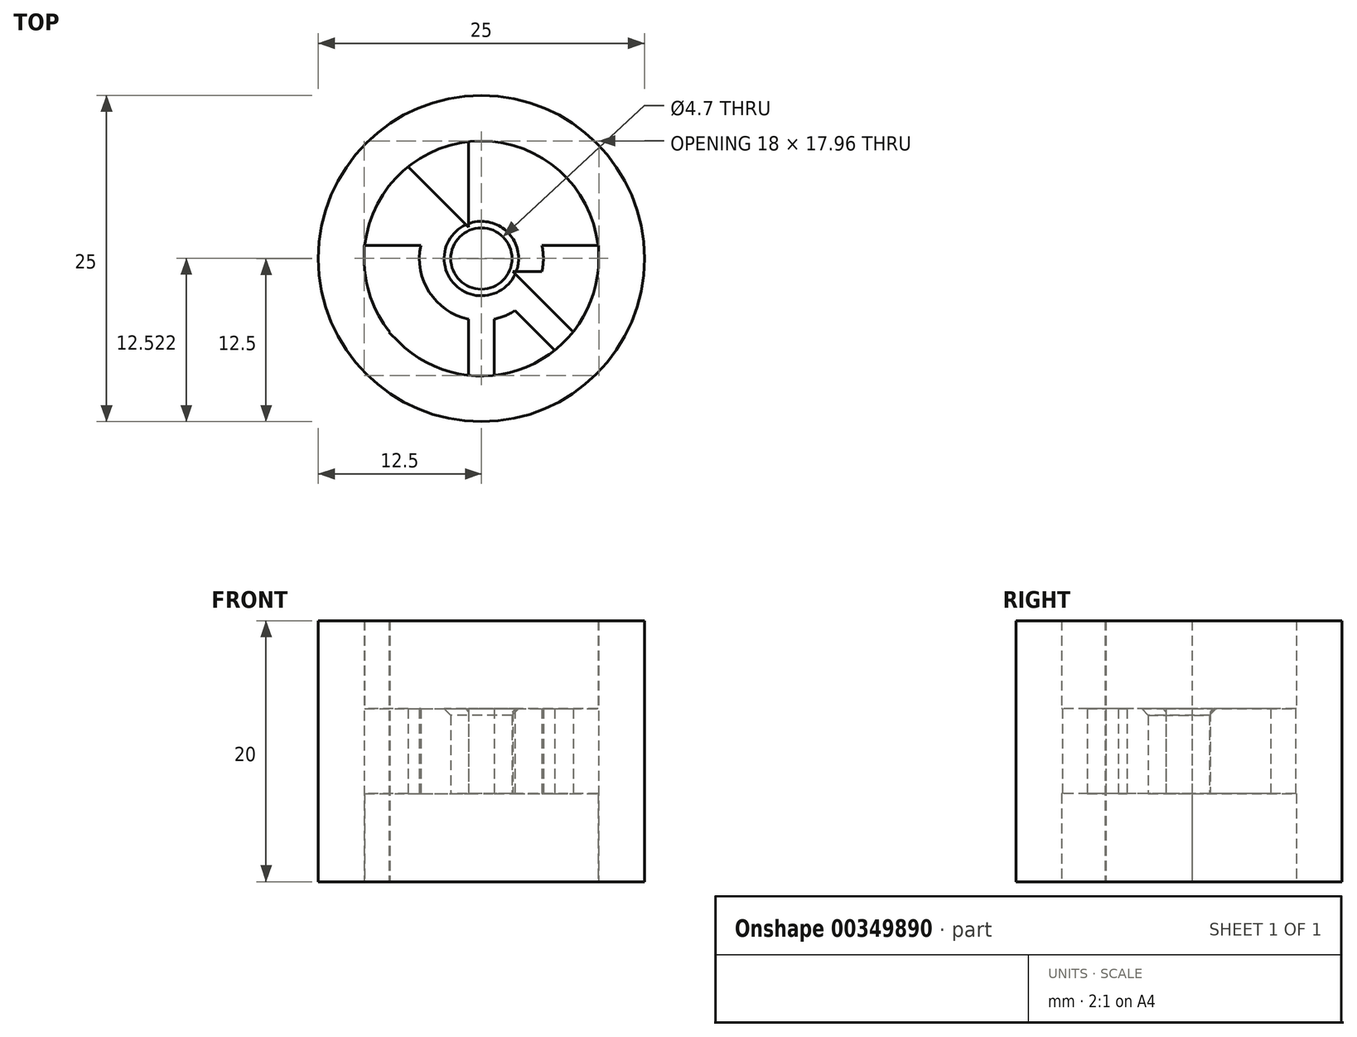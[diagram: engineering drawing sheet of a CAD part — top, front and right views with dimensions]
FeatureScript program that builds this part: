
annotation { "Feature Type Name" : "Feature", "Feature Type Description" : "" }
export const myFeature = defineFeature(function(context is Context, id is Id, definition is map)
    precondition{}
    {
        {
            var Q0;
            Q0=qCreatedBy(makeId("Top.planeOp"),FACE);
            var sketch = newSketch(context, id + "F0", { "sketchPlane" : qUnion([Q0])});
            skCircle(sketch, "E0", {"center": v(0, 0) * mm, "radius": 2.35 * mm});
            skCircle(sketch, "E1", {"center": v(0, 0) * mm, "radius": 12.5 * mm});
            skCircle(sketch, "E2", {"center": v(0, 0) * mm, "radius": 9 * mm});
            skCircle(sketch, "E3", {"center": v(0, 0) * mm, "radius": 4.75 * mm});
            skPoint(sketch, "E4", {"position": v(0, 9) * mm});
            skPoint(sketch, "E5", {"position": v(0, -9) * mm});
            skPoint(sketch, "E6", {"position": v(9, 0) * mm});
            skPoint(sketch, "E7", {"position": v(-9, 0) * mm});
            skLineSegment(sketch, "E8.bottom", {"start": v(-1, 9) * mm, "end": v(1, 9) * mm});
            skLineSegment(sketch, "E8.top", {"start": v(-1, -9) * mm, "end": v(1, -9) * mm});
            skLineSegment(sketch, "E8.left", {"start": v(-1, 9) * mm, "end": v(-1, -9) * mm});
            skLineSegment(sketch, "E8.right", {"start": v(1, 9) * mm, "end": v(1, -9) * mm});
            skLineSegment(sketch, "E9.bottom", {"start": v(-9, 1) * mm, "end": v(9, 1) * mm});
            skLineSegment(sketch, "E9.top", {"start": v(-9, -1) * mm, "end": v(9, -1) * mm});
            skLineSegment(sketch, "E9.left", {"start": v(-9, 1) * mm, "end": v(-9, -1) * mm});
            skLineSegment(sketch, "E9.right", {"start": v(9, 1) * mm, "end": v(9, -1) * mm});
            skLineSegment(sketch, "E10", {"start": v(0, 0) * mm, "end": v(-6.36, -6.36) * mm, "construction": true});
            skLineSegment(sketch, "E11", {"start": v(0, 0) * mm, "end": v(-6.36, 6.36) * mm, "construction": true});
            skLineSegment(sketch, "E12", {"start": v(0, 0) * mm, "end": v(6.36, 6.36) * mm, "construction": true});
            skLineSegment(sketch, "E13", {"start": v(0, 0) * mm, "end": v(6.36, -6.36) * mm, "construction": true});
            skPoint(sketch, "E14", {"position": v(-1, -1) * mm});
            skPoint(sketch, "E15", {"position": v(-1, 1) * mm});
            skLineSegment(sketch, "E16", {"start": v(-7.07, -5.66) * mm, "end": v(-5.66, -7.07) * mm});
            skPoint(sketch, "E17", {"position": v(-6.36, -6.36) * mm});
            skLineSegment(sketch, "E18", {"start": v(5.66, -7.07) * mm, "end": v(7.07, -5.66) * mm});
            skPoint(sketch, "E19", {"position": v(6.36, -6.36) * mm});
            skPoint(sketch, "E20", {"position": v(6.36, 6.36) * mm});
            skLineSegment(sketch, "E21", {"start": v(5.66, 7.07) * mm, "end": v(7.07, 5.66) * mm});
            skLineSegment(sketch, "E22", {"start": v(-7.07, -5.66) * mm, "end": v(5.66, 7.07) * mm});
            skLineSegment(sketch, "E23", {"start": v(7.07, 5.66) * mm, "end": v(-5.66, -7.07) * mm});
            skLineSegment(sketch, "E24", {"start": v(-7.07, 5.66) * mm, "end": v(-5.66, 7.07) * mm});
            skPoint(sketch, "E25", {"position": v(-6.36, 6.36) * mm});
            skLineSegment(sketch, "E26", {"start": v(-7.07, 5.66) * mm, "end": v(5.66, -7.07) * mm});
            skLineSegment(sketch, "E27", {"start": v(-5.66, 7.07) * mm, "end": v(7.07, -5.66) * mm});
            skSolve(sketch);
        }
        {
            var Q0;
            {var subQ0=sQuery(id+"F0.wireOp",EDGE,"E8.right");var subQ5=sQuery(id+"F0.wireOp",EDGE,"E2");var subQ6=makeQuery(id+"F0.imprint","INTERSECT",VERTEX,{"disambiguationData":[OD(0.0)],"derivedFrom":[subQ5,subQ0]});Q0=makeQuery(id+"F0.imprint","IMPRINT",FACE,{"disambiguationData":[TD([[makeQuery(id+"F0.imprint","IMPRINT",EDGE,{"disambiguationData":[TD([[subQ6,-1.0]])],"derivedFrom":subQ5}),1.0]])]});}
            var Q1;
            {var subQ3=sQuery(id+"F0.wireOp",EDGE,"E22");var subQ7=sQuery(id+"F0.wireOp",EDGE,"E0");var subQ8=makeQuery(id+"F0.imprint","INTERSECT",VERTEX,{"disambiguationData":[OD(0.0)],"derivedFrom":[subQ7,subQ3]});Q1=makeQuery(id+"F0.imprint","IMPRINT",FACE,{"disambiguationData":[TD([[makeQuery(id+"F0.imprint","IMPRINT",EDGE,{"disambiguationData":[TD([[subQ8,-1.0]])],"derivedFrom":subQ7}),-1.0]])]});}
            var Q2;
            {var subQ0=sQuery(id+"F0.wireOp",EDGE,"E27");var subQ1=sQuery(id+"F0.wireOp",EDGE,"E0");var subQ2=makeQuery(id+"F0.imprint","INTERSECT",VERTEX,{"disambiguationData":[OD(0.0)],"derivedFrom":[subQ1,subQ0]});Q2=makeQuery(id+"F0.imprint","IMPRINT",FACE,{"disambiguationData":[TD([[makeQuery(id+"F0.imprint","IMPRINT",EDGE,{"disambiguationData":[TD([[subQ2,-1.0]])],"derivedFrom":subQ1}),-1.0]])]});}
            var Q3;
            {var subQ0=sQuery(id+"F0.wireOp",EDGE,"E8.right");var subQ1=sQuery(id+"F0.wireOp",EDGE,"E0");var subQ2=makeQuery(id+"F0.imprint","INTERSECT",VERTEX,{"disambiguationData":[OD(0.0)],"derivedFrom":[subQ1,subQ0]});Q3=makeQuery(id+"F0.imprint","IMPRINT",FACE,{"disambiguationData":[TD([[makeQuery(id+"F0.imprint","IMPRINT",EDGE,{"disambiguationData":[TD([[subQ2,-1.0]])],"derivedFrom":subQ1}),-1.0]])]});}
            var Q4;
            {var subQ1=sQuery(id+"F0.wireOp",EDGE,"E0");var subQ9=sQuery(id+"F0.wireOp",EDGE,"E9.bottom");var subQ10=makeQuery(id+"F0.imprint","INTERSECT",VERTEX,{"disambiguationData":[OD(0.0)],"derivedFrom":[subQ1,subQ9]});Q4=makeQuery(id+"F0.imprint","IMPRINT",FACE,{"disambiguationData":[TD([[makeQuery(id+"F0.imprint","IMPRINT",EDGE,{"disambiguationData":[TD([[subQ10,-1.0]])],"derivedFrom":subQ1}),-1.0]])]});}
            var Q5;
            {var subQ3=sQuery(id+"F0.wireOp",EDGE,"E23");var subQ9=sQuery(id+"F0.wireOp",EDGE,"E0");var subQ10=makeQuery(id+"F0.imprint","INTERSECT",VERTEX,{"disambiguationData":[OD(0.0)],"derivedFrom":[subQ9,subQ3]});Q5=makeQuery(id+"F0.imprint","IMPRINT",FACE,{"disambiguationData":[TD([[makeQuery(id+"F0.imprint","IMPRINT",EDGE,{"disambiguationData":[TD([[subQ10,1.0]])],"derivedFrom":subQ9}),-1.0]])]});}
            var Q6;
            {var subQ0=sQuery(id+"F0.wireOp",EDGE,"E9.bottom");var subQ1=sQuery(id+"F0.wireOp",EDGE,"E0");var subQ2=makeQuery(id+"F0.imprint","INTERSECT",VERTEX,{"disambiguationData":[OD(0.0)],"derivedFrom":[subQ1,subQ0]});Q6=makeQuery(id+"F0.imprint","IMPRINT",FACE,{"disambiguationData":[TD([[makeQuery(id+"F0.imprint","IMPRINT",EDGE,{"disambiguationData":[TD([[subQ2,1.0]])],"derivedFrom":subQ1}),-1.0]])]});}
            var Q7;
            {var subQ1=sQuery(id+"F0.wireOp",EDGE,"E0");var subQ9=sQuery(id+"F0.wireOp",EDGE,"E8.right");var subQ10=makeQuery(id+"F0.imprint","INTERSECT",VERTEX,{"disambiguationData":[OD(1.0)],"derivedFrom":[subQ1,subQ9]});Q7=makeQuery(id+"F0.imprint","IMPRINT",FACE,{"disambiguationData":[TD([[makeQuery(id+"F0.imprint","IMPRINT",EDGE,{"disambiguationData":[TD([[subQ10,-1.0]])],"derivedFrom":subQ1}),-1.0]])]});}
            var Q8;
            {var subQ0=sQuery(id+"F0.wireOp",EDGE,"E9.top");var subQ1=sQuery(id+"F0.wireOp",EDGE,"E0");var subQ2=makeQuery(id+"F0.imprint","INTERSECT",VERTEX,{"disambiguationData":[OD(1.0)],"derivedFrom":[subQ1,subQ0]});Q8=makeQuery(id+"F0.imprint","IMPRINT",FACE,{"disambiguationData":[TD([[makeQuery(id+"F0.imprint","IMPRINT",EDGE,{"disambiguationData":[TD([[subQ2,-1.0]])],"derivedFrom":subQ1}),-1.0]])]});}
            var Q9;
            {var subQ0=sQuery(id+"F0.wireOp",EDGE,"E26");var subQ1=sQuery(id+"F0.wireOp",EDGE,"E0");var subQ2=makeQuery(id+"F0.imprint","INTERSECT",VERTEX,{"disambiguationData":[OD(1.0)],"derivedFrom":[subQ1,subQ0]});Q9=makeQuery(id+"F0.imprint","IMPRINT",FACE,{"disambiguationData":[TD([[makeQuery(id+"F0.imprint","IMPRINT",EDGE,{"disambiguationData":[TD([[subQ2,-1.0]])],"derivedFrom":subQ1}),-1.0]])]});}
            var Q10;
            {var subQ0=sQuery(id+"F0.wireOp",EDGE,"E8.left");var subQ1=sQuery(id+"F0.wireOp",EDGE,"E0");var subQ2=makeQuery(id+"F0.imprint","INTERSECT",VERTEX,{"disambiguationData":[OD(0.0)],"derivedFrom":[subQ1,subQ0]});Q10=makeQuery(id+"F0.imprint","IMPRINT",FACE,{"disambiguationData":[TD([[makeQuery(id+"F0.imprint","IMPRINT",EDGE,{"disambiguationData":[TD([[subQ2,-1.0]])],"derivedFrom":subQ1}),-1.0]])]});}
            var Q11;
            {var subQ3=sQuery(id+"F0.wireOp",EDGE,"E26");var subQ9=sQuery(id+"F0.wireOp",EDGE,"E0");var subQ10=makeQuery(id+"F0.imprint","INTERSECT",VERTEX,{"disambiguationData":[OD(0.0)],"derivedFrom":[subQ9,subQ3]});Q11=makeQuery(id+"F0.imprint","IMPRINT",FACE,{"disambiguationData":[TD([[makeQuery(id+"F0.imprint","IMPRINT",EDGE,{"disambiguationData":[TD([[subQ10,-1.0]])],"derivedFrom":subQ9}),-1.0]])]});}
            var Q12;
            {var subQ0=sQuery(id+"F0.wireOp",EDGE,"E9.top");var subQ1=sQuery(id+"F0.wireOp",EDGE,"E0");var subQ2=makeQuery(id+"F0.imprint","INTERSECT",VERTEX,{"disambiguationData":[OD(0.0)],"derivedFrom":[subQ1,subQ0]});Q12=makeQuery(id+"F0.imprint","IMPRINT",FACE,{"disambiguationData":[TD([[makeQuery(id+"F0.imprint","IMPRINT",EDGE,{"disambiguationData":[TD([[subQ2,-1.0]])],"derivedFrom":subQ1}),-1.0]])]});}
            var Q13;
            {var subQ0=sQuery(id+"F0.wireOp",EDGE,"E9.bottom");var subQ1=sQuery(id+"F0.wireOp",EDGE,"E0");var subQ2=makeQuery(id+"F0.imprint","INTERSECT",VERTEX,{"disambiguationData":[OD(1.0)],"derivedFrom":[subQ1,subQ0]});Q13=makeQuery(id+"F0.imprint","IMPRINT",FACE,{"disambiguationData":[TD([[makeQuery(id+"F0.imprint","IMPRINT",EDGE,{"disambiguationData":[TD([[subQ2,-1.0]])],"derivedFrom":subQ1}),-1.0]])]});}
            var Q14;
            {var subQ0=sQuery(id+"F0.wireOp",EDGE,"E22");var subQ1=sQuery(id+"F0.wireOp",EDGE,"E0");var subQ2=makeQuery(id+"F0.imprint","INTERSECT",VERTEX,{"disambiguationData":[OD(1.0)],"derivedFrom":[subQ1,subQ0]});Q14=makeQuery(id+"F0.imprint","IMPRINT",FACE,{"disambiguationData":[TD([[makeQuery(id+"F0.imprint","IMPRINT",EDGE,{"disambiguationData":[TD([[subQ2,-1.0]])],"derivedFrom":subQ1}),-1.0]])]});}
            var Q15;
            {var subQ0=sQuery(id+"F0.wireOp",EDGE,"E8.left");var subQ1=sQuery(id+"F0.wireOp",EDGE,"E0");var subQ2=makeQuery(id+"F0.imprint","INTERSECT",VERTEX,{"disambiguationData":[OD(1.0)],"derivedFrom":[subQ1,subQ0]});Q15=makeQuery(id+"F0.imprint","IMPRINT",FACE,{"disambiguationData":[TD([[makeQuery(id+"F0.imprint","IMPRINT",EDGE,{"disambiguationData":[TD([[subQ2,-1.0]])],"derivedFrom":subQ1}),-1.0]])]});}
            var Q16;
            {var subQ7=sQuery(id+"F0.wireOp",EDGE,"E23");var subQ9=sQuery(id+"F0.wireOp",EDGE,"E0");var subQ10=makeQuery(id+"F0.imprint","INTERSECT",VERTEX,{"disambiguationData":[OD(1.0)],"derivedFrom":[subQ9,subQ7]});Q16=makeQuery(id+"F0.imprint","IMPRINT",FACE,{"disambiguationData":[TD([[makeQuery(id+"F0.imprint","IMPRINT",EDGE,{"disambiguationData":[TD([[subQ10,-1.0]])],"derivedFrom":subQ9}),-1.0]])]});}
            var Q17;
            {var subQ0=sQuery(id+"F0.wireOp",EDGE,"E23");var subQ5=sQuery(id+"F0.wireOp",EDGE,"E2");var subQ8=makeQuery(id+"F0.imprint","INTERSECT",VERTEX,{"disambiguationData":[OD(0.0)],"derivedFrom":[subQ5,subQ0]});Q17=makeQuery(id+"F0.imprint","IMPRINT",FACE,{"disambiguationData":[TD([[makeQuery(id+"F0.imprint","IMPRINT",EDGE,{"disambiguationData":[TD([[subQ8,-1.0]])],"derivedFrom":subQ5}),1.0]])]});}
            var Q18;
            {var subQ0=sQuery(id+"F0.wireOp",EDGE,"E9.bottom");var subQ1=sQuery(id+"F0.wireOp",EDGE,"E2");var subQ2=makeQuery(id+"F0.imprint","INTERSECT",VERTEX,{"disambiguationData":[OD(0.0)],"derivedFrom":[subQ1,subQ0]});Q18=makeQuery(id+"F0.imprint","IMPRINT",FACE,{"disambiguationData":[TD([[makeQuery(id+"F0.imprint","IMPRINT",EDGE,{"disambiguationData":[TD([[subQ2,1.0]])],"derivedFrom":subQ1}),1.0]])]});}
            var Q19;
            {var subQ0=sQuery(id+"F0.wireOp",EDGE,"E26");var subQ5=sQuery(id+"F0.wireOp",EDGE,"E2");var subQ8=makeQuery(id+"F0.imprint","INTERSECT",VERTEX,{"disambiguationData":[OD(1.0)],"derivedFrom":[subQ5,subQ0]});Q19=makeQuery(id+"F0.imprint","IMPRINT",FACE,{"disambiguationData":[TD([[makeQuery(id+"F0.imprint","IMPRINT",EDGE,{"disambiguationData":[TD([[subQ8,-1.0]])],"derivedFrom":subQ5}),1.0]])]});}
            var Q20;
            {var subQ0=sQuery(id+"F0.wireOp",EDGE,"E8.left");var subQ1=sQuery(id+"F0.wireOp",EDGE,"E2");var subQ2=makeQuery(id+"F0.imprint","INTERSECT",VERTEX,{"disambiguationData":[OD(1.0)],"derivedFrom":[subQ1,subQ0]});Q20=makeQuery(id+"F0.imprint","IMPRINT",FACE,{"disambiguationData":[TD([[makeQuery(id+"F0.imprint","IMPRINT",EDGE,{"disambiguationData":[TD([[subQ2,-1.0]])],"derivedFrom":subQ1}),1.0]])]});}
            var Q21;
            {var subQ0=sQuery(id+"F0.wireOp",EDGE,"E22");var subQ1=sQuery(id+"F0.wireOp",EDGE,"E2");var subQ2=makeQuery(id+"F0.imprint","INTERSECT",VERTEX,{"disambiguationData":[OD(1.0)],"derivedFrom":[subQ1,subQ0]});Q21=makeQuery(id+"F0.imprint","IMPRINT",FACE,{"disambiguationData":[TD([[makeQuery(id+"F0.imprint","IMPRINT",EDGE,{"disambiguationData":[TD([[subQ2,-1.0]])],"derivedFrom":subQ1}),1.0]])]});}
            var Q22;
            {var subQ0=sQuery(id+"F0.wireOp",EDGE,"E2");var subQ4=sQuery(id+"F0.wireOp",EDGE,"E9.bottom");var subQ5=makeQuery(id+"F0.imprint","INTERSECT",VERTEX,{"disambiguationData":[OD(1.0)],"derivedFrom":[subQ0,subQ4]});Q22=makeQuery(id+"F0.imprint","IMPRINT",FACE,{"disambiguationData":[TD([[makeQuery(id+"F0.imprint","IMPRINT",EDGE,{"disambiguationData":[TD([[subQ5,-1.0]])],"derivedFrom":subQ0}),1.0]])]});}
            var Q23;
            {var subQ1=sQuery(id+"F0.wireOp",EDGE,"E2");var subQ5=sQuery(id+"F0.wireOp",EDGE,"E27");var subQ8=makeQuery(id+"F0.imprint","INTERSECT",VERTEX,{"disambiguationData":[OD(0.0)],"derivedFrom":[subQ1,subQ5]});Q23=makeQuery(id+"F0.imprint","IMPRINT",FACE,{"disambiguationData":[TD([[makeQuery(id+"F0.imprint","IMPRINT",EDGE,{"disambiguationData":[TD([[subQ8,-1.0]])],"derivedFrom":subQ1}),1.0]])]});}
            var Q24;
            {var subQ0=sQuery(id+"F0.wireOp",EDGE,"E22");var subQ1=sQuery(id+"F0.wireOp",EDGE,"E3");var subQ2=makeQuery(id+"F0.imprint","INTERSECT",VERTEX,{"disambiguationData":[OD(0.0)],"derivedFrom":[subQ1,subQ0]});Q24=makeQuery(id+"F0.imprint","IMPRINT",FACE,{"disambiguationData":[TD([[makeQuery(id+"F0.imprint","IMPRINT",EDGE,{"disambiguationData":[TD([[subQ2,-1.0]])],"derivedFrom":subQ1}),1.0]])]});}
            var Q25;
            {var subQ0=sQuery(id+"F0.wireOp",EDGE,"E23");var subQ1=sQuery(id+"F0.wireOp",EDGE,"E3");var subQ2=makeQuery(id+"F0.imprint","INTERSECT",VERTEX,{"disambiguationData":[OD(0.0)],"derivedFrom":[subQ1,subQ0]});Q25=makeQuery(id+"F0.imprint","IMPRINT",FACE,{"disambiguationData":[TD([[makeQuery(id+"F0.imprint","IMPRINT",EDGE,{"disambiguationData":[TD([[subQ2,1.0]])],"derivedFrom":subQ1}),1.0]])]});}
            var Q26;
            {var subQ0=sQuery(id+"F0.wireOp",EDGE,"E27");var subQ1=sQuery(id+"F0.wireOp",EDGE,"E3");var subQ2=makeQuery(id+"F0.imprint","INTERSECT",VERTEX,{"disambiguationData":[OD(1.0)],"derivedFrom":[subQ1,subQ0]});Q26=makeQuery(id+"F0.imprint","IMPRINT",FACE,{"disambiguationData":[TD([[makeQuery(id+"F0.imprint","IMPRINT",EDGE,{"disambiguationData":[TD([[subQ2,-1.0]])],"derivedFrom":subQ1}),1.0]])]});}
            var Q27;
            {var subQ0=sQuery(id+"F0.wireOp",EDGE,"E8.right");var subQ1=sQuery(id+"F0.wireOp",EDGE,"E3");var subQ2=makeQuery(id+"F0.imprint","INTERSECT",VERTEX,{"disambiguationData":[OD(1.0)],"derivedFrom":[subQ1,subQ0]});Q27=makeQuery(id+"F0.imprint","IMPRINT",FACE,{"disambiguationData":[TD([[makeQuery(id+"F0.imprint","IMPRINT",EDGE,{"disambiguationData":[TD([[subQ2,-1.0]])],"derivedFrom":subQ1}),1.0]])]});}
            var Q28;
            {var subQ0=sQuery(id+"F0.wireOp",EDGE,"E23");var subQ1=sQuery(id+"F0.wireOp",EDGE,"E3");var subQ2=makeQuery(id+"F0.imprint","INTERSECT",VERTEX,{"disambiguationData":[OD(1.0)],"derivedFrom":[subQ1,subQ0]});Q28=makeQuery(id+"F0.imprint","IMPRINT",FACE,{"disambiguationData":[TD([[makeQuery(id+"F0.imprint","IMPRINT",EDGE,{"disambiguationData":[TD([[subQ2,-1.0]])],"derivedFrom":subQ1}),1.0]])]});}
            var Q29;
            {var subQ0=sQuery(id+"F0.wireOp",EDGE,"E9.top");var subQ1=sQuery(id+"F0.wireOp",EDGE,"E3");var subQ2=makeQuery(id+"F0.imprint","INTERSECT",VERTEX,{"disambiguationData":[OD(0.0)],"derivedFrom":[subQ1,subQ0]});Q29=makeQuery(id+"F0.imprint","IMPRINT",FACE,{"disambiguationData":[TD([[makeQuery(id+"F0.imprint","IMPRINT",EDGE,{"disambiguationData":[TD([[subQ2,-1.0]])],"derivedFrom":subQ1}),1.0]])]});}
            var Q30;
            {var subQ0=sQuery(id+"F0.wireOp",EDGE,"E26");var subQ1=sQuery(id+"F0.wireOp",EDGE,"E3");var subQ2=makeQuery(id+"F0.imprint","INTERSECT",VERTEX,{"disambiguationData":[OD(0.0)],"derivedFrom":[subQ1,subQ0]});Q30=makeQuery(id+"F0.imprint","IMPRINT",FACE,{"disambiguationData":[TD([[makeQuery(id+"F0.imprint","IMPRINT",EDGE,{"disambiguationData":[TD([[subQ2,-1.0]])],"derivedFrom":subQ1}),1.0]])]});}
            var Q31;
            {var subQ0=sQuery(id+"F0.wireOp",EDGE,"E8.left");var subQ1=sQuery(id+"F0.wireOp",EDGE,"E3");var subQ2=makeQuery(id+"F0.imprint","INTERSECT",VERTEX,{"disambiguationData":[OD(0.0)],"derivedFrom":[subQ1,subQ0]});Q31=makeQuery(id+"F0.imprint","IMPRINT",FACE,{"disambiguationData":[TD([[makeQuery(id+"F0.imprint","IMPRINT",EDGE,{"disambiguationData":[TD([[subQ2,-1.0]])],"derivedFrom":subQ1}),1.0]])]});}
            var Q32;
            {var subQ0=sQuery(id+"F0.wireOp",EDGE,"E9.bottom");var subQ1=sQuery(id+"F0.wireOp",EDGE,"E2");var subQ2=makeQuery(id+"F0.imprint","INTERSECT",VERTEX,{"disambiguationData":[OD(1.0)],"derivedFrom":[subQ1,subQ0]});Q32=makeQuery(id+"F0.imprint","IMPRINT",FACE,{"disambiguationData":[TD([[makeQuery(id+"F0.imprint","IMPRINT",EDGE,{"disambiguationData":[TD([[subQ2,-1.0]])],"derivedFrom":subQ1}),-1.0]])]});}
            var Q33;
            {var subQ0=sQuery(id+"F0.wireOp",EDGE,"E9.left");var subQ1=sQuery(id+"F0.wireOp",EDGE,"E2");var subQ2=makeQuery(id+"F0.imprint","INTERSECT",VERTEX,{"derivedFrom":[subQ1,subQ0]});Q33=makeQuery(id+"F0.imprint","IMPRINT",FACE,{"disambiguationData":[TD([[makeQuery(id+"F0.imprint","IMPRINT",EDGE,{"disambiguationData":[TD([[subQ2,-1.0]])],"derivedFrom":subQ1}),-1.0]])]});}
            var Q34;
            {var subQ0=sQuery(id+"F0.wireOp",EDGE,"E22");var subQ1=sQuery(id+"F0.wireOp",EDGE,"E2");var subQ2=makeQuery(id+"F0.imprint","INTERSECT",VERTEX,{"disambiguationData":[OD(1.0)],"derivedFrom":[subQ1,subQ0]});Q34=makeQuery(id+"F0.imprint","IMPRINT",FACE,{"disambiguationData":[TD([[makeQuery(id+"F0.imprint","IMPRINT",EDGE,{"disambiguationData":[TD([[subQ2,-1.0]])],"derivedFrom":subQ1}),-1.0]])]});}
            var Q35;
            {var subQ0=sQuery(id+"F0.wireOp",EDGE,"E16");var subQ1=sQuery(id+"F0.wireOp",EDGE,"E2");var subQ2=makeQuery(id+"F0.imprint","INTERSECT",VERTEX,{"derivedFrom":[subQ1,subQ0]});Q35=makeQuery(id+"F0.imprint","IMPRINT",FACE,{"disambiguationData":[TD([[makeQuery(id+"F0.imprint","IMPRINT",EDGE,{"disambiguationData":[TD([[subQ2,-1.0]])],"derivedFrom":subQ1}),-1.0]])]});}
            var Q36;
            {var subQ0=sQuery(id+"F0.wireOp",EDGE,"E8.top");var subQ1=sQuery(id+"F0.wireOp",EDGE,"E2");var subQ2=makeQuery(id+"F0.imprint","INTERSECT",VERTEX,{"derivedFrom":[subQ1,subQ0]});Q36=makeQuery(id+"F0.imprint","IMPRINT",FACE,{"disambiguationData":[TD([[makeQuery(id+"F0.imprint","IMPRINT",EDGE,{"disambiguationData":[TD([[subQ2,-1.0]])],"derivedFrom":subQ1}),-1.0]])]});}
            var Q37;
            {var subQ0=sQuery(id+"F0.wireOp",EDGE,"E8.left");var subQ1=sQuery(id+"F0.wireOp",EDGE,"E2");var subQ2=makeQuery(id+"F0.imprint","INTERSECT",VERTEX,{"disambiguationData":[OD(1.0)],"derivedFrom":[subQ1,subQ0]});Q37=makeQuery(id+"F0.imprint","IMPRINT",FACE,{"disambiguationData":[TD([[makeQuery(id+"F0.imprint","IMPRINT",EDGE,{"disambiguationData":[TD([[subQ2,-1.0]])],"derivedFrom":subQ1}),-1.0]])]});}
            var Q38;
            {var subQ0=sQuery(id+"F0.wireOp",EDGE,"E18");var subQ1=sQuery(id+"F0.wireOp",EDGE,"E2");var subQ2=makeQuery(id+"F0.imprint","INTERSECT",VERTEX,{"derivedFrom":[subQ1,subQ0]});Q38=makeQuery(id+"F0.imprint","IMPRINT",FACE,{"disambiguationData":[TD([[makeQuery(id+"F0.imprint","IMPRINT",EDGE,{"disambiguationData":[TD([[subQ2,-1.0]])],"derivedFrom":subQ1}),-1.0]])]});}
            var Q39;
            {var subQ0=sQuery(id+"F0.wireOp",EDGE,"E26");var subQ1=sQuery(id+"F0.wireOp",EDGE,"E2");var subQ2=makeQuery(id+"F0.imprint","INTERSECT",VERTEX,{"disambiguationData":[OD(1.0)],"derivedFrom":[subQ1,subQ0]});Q39=makeQuery(id+"F0.imprint","IMPRINT",FACE,{"disambiguationData":[TD([[makeQuery(id+"F0.imprint","IMPRINT",EDGE,{"disambiguationData":[TD([[subQ2,-1.0]])],"derivedFrom":subQ1}),-1.0]])]});}
            var Q40;
            {var subQ0=sQuery(id+"F0.wireOp",EDGE,"E9.bottom");var subQ1=sQuery(id+"F0.wireOp",EDGE,"E2");var subQ2=makeQuery(id+"F0.imprint","INTERSECT",VERTEX,{"disambiguationData":[OD(0.0)],"derivedFrom":[subQ1,subQ0]});Q40=makeQuery(id+"F0.imprint","IMPRINT",FACE,{"disambiguationData":[TD([[makeQuery(id+"F0.imprint","IMPRINT",EDGE,{"disambiguationData":[TD([[subQ2,1.0]])],"derivedFrom":subQ1}),-1.0]])]});}
            var Q41;
            {var subQ0=sQuery(id+"F0.wireOp",EDGE,"E9.right");var subQ1=sQuery(id+"F0.wireOp",EDGE,"E2");var subQ2=makeQuery(id+"F0.imprint","INTERSECT",VERTEX,{"derivedFrom":[subQ1,subQ0]});Q41=makeQuery(id+"F0.imprint","IMPRINT",FACE,{"disambiguationData":[TD([[makeQuery(id+"F0.imprint","IMPRINT",EDGE,{"disambiguationData":[TD([[subQ2,1.0]])],"derivedFrom":subQ1}),-1.0]])]});}
            var Q42;
            {var subQ0=sQuery(id+"F0.wireOp",EDGE,"E21");var subQ1=sQuery(id+"F0.wireOp",EDGE,"E2");var subQ2=makeQuery(id+"F0.imprint","INTERSECT",VERTEX,{"derivedFrom":[subQ1,subQ0]});Q42=makeQuery(id+"F0.imprint","IMPRINT",FACE,{"disambiguationData":[TD([[makeQuery(id+"F0.imprint","IMPRINT",EDGE,{"disambiguationData":[TD([[subQ2,-1.0]])],"derivedFrom":subQ1}),-1.0]])]});}
            var Q43;
            {var subQ0=sQuery(id+"F0.wireOp",EDGE,"E23");var subQ1=sQuery(id+"F0.wireOp",EDGE,"E2");var subQ2=makeQuery(id+"F0.imprint","INTERSECT",VERTEX,{"disambiguationData":[OD(0.0)],"derivedFrom":[subQ1,subQ0]});Q43=makeQuery(id+"F0.imprint","IMPRINT",FACE,{"disambiguationData":[TD([[makeQuery(id+"F0.imprint","IMPRINT",EDGE,{"disambiguationData":[TD([[subQ2,-1.0]])],"derivedFrom":subQ1}),-1.0]])]});}
            var Q44;
            {var subQ0=sQuery(id+"F0.wireOp",EDGE,"E8.right");var subQ1=sQuery(id+"F0.wireOp",EDGE,"E2");var subQ2=makeQuery(id+"F0.imprint","INTERSECT",VERTEX,{"disambiguationData":[OD(0.0)],"derivedFrom":[subQ1,subQ0]});Q44=makeQuery(id+"F0.imprint","IMPRINT",FACE,{"disambiguationData":[TD([[makeQuery(id+"F0.imprint","IMPRINT",EDGE,{"disambiguationData":[TD([[subQ2,-1.0]])],"derivedFrom":subQ1}),-1.0]])]});}
            var Q45;
            {var subQ0=sQuery(id+"F0.wireOp",EDGE,"E8.bottom");var subQ1=sQuery(id+"F0.wireOp",EDGE,"E2");var subQ2=makeQuery(id+"F0.imprint","INTERSECT",VERTEX,{"derivedFrom":[subQ1,subQ0]});Q45=makeQuery(id+"F0.imprint","IMPRINT",FACE,{"disambiguationData":[TD([[makeQuery(id+"F0.imprint","IMPRINT",EDGE,{"disambiguationData":[TD([[subQ2,-1.0]])],"derivedFrom":subQ1}),-1.0]])]});}
            var Q46;
            {var subQ0=sQuery(id+"F0.wireOp",EDGE,"E27");var subQ1=sQuery(id+"F0.wireOp",EDGE,"E2");var subQ2=makeQuery(id+"F0.imprint","INTERSECT",VERTEX,{"disambiguationData":[OD(0.0)],"derivedFrom":[subQ1,subQ0]});Q46=makeQuery(id+"F0.imprint","IMPRINT",FACE,{"disambiguationData":[TD([[makeQuery(id+"F0.imprint","IMPRINT",EDGE,{"disambiguationData":[TD([[subQ2,-1.0]])],"derivedFrom":subQ1}),-1.0]])]});}
            var Q47;
            {var subQ0=sQuery(id+"F0.wireOp",EDGE,"E24");var subQ1=sQuery(id+"F0.wireOp",EDGE,"E2");var subQ2=makeQuery(id+"F0.imprint","INTERSECT",VERTEX,{"derivedFrom":[subQ1,subQ0]});Q47=makeQuery(id+"F0.imprint","IMPRINT",FACE,{"disambiguationData":[TD([[makeQuery(id+"F0.imprint","IMPRINT",EDGE,{"disambiguationData":[TD([[subQ2,-1.0]])],"derivedFrom":subQ1}),-1.0]])]});}
            extrude(context, id + "F1", {"entities" : qUnion([Q0, Q1, Q2, Q3, Q4, Q5, Q6, Q7, Q8, Q9, Q10, Q11, Q12, Q13, Q14, Q15, Q16, Q17, Q18, Q19, Q20, Q21, Q22, Q23, Q24, Q25, Q26, Q27, Q28, Q29, Q30, Q31, Q32, Q33, Q34, Q35, Q36, Q37, Q38, Q39, Q40, Q41, Q42, Q43, Q44, Q45, Q46, Q47]), "endBound" : BoundingType.SYMMETRIC, "depth" : 6.5 * mm});
        }
        {
            var Q0;
            Q0=makeQuery(id+"F0.imprint","IMPRINT",FACE,{"disambiguationData":[TD([[makeQuery(id+"F0.imprint","IMPRINT",EDGE,{"derivedFrom":sQuery(id+"F0.wireOp",EDGE,"E1")}),1.0]])]});
            var Q1;
            {var subQ0=sQuery(id+"F0.wireOp",EDGE,"E8.bottom");var subQ1=sQuery(id+"F0.wireOp",EDGE,"E2");var subQ2=makeQuery(id+"F0.imprint","INTERSECT",VERTEX,{"derivedFrom":[subQ1,subQ0]});Q1=makeQuery(id+"F0.imprint","IMPRINT",FACE,{"disambiguationData":[TD([[makeQuery(id+"F0.imprint","IMPRINT",EDGE,{"disambiguationData":[TD([[subQ2,-1.0]])],"derivedFrom":subQ1}),-1.0]])]});}
            var Q2;
            {var subQ0=sQuery(id+"F0.wireOp",EDGE,"E8.right");var subQ1=sQuery(id+"F0.wireOp",EDGE,"E2");var subQ2=makeQuery(id+"F0.imprint","INTERSECT",VERTEX,{"disambiguationData":[OD(0.0)],"derivedFrom":[subQ1,subQ0]});Q2=makeQuery(id+"F0.imprint","IMPRINT",FACE,{"disambiguationData":[TD([[makeQuery(id+"F0.imprint","IMPRINT",EDGE,{"disambiguationData":[TD([[subQ2,-1.0]])],"derivedFrom":subQ1}),-1.0]])]});}
            var Q3;
            {var subQ0=sQuery(id+"F0.wireOp",EDGE,"E27");var subQ1=sQuery(id+"F0.wireOp",EDGE,"E2");var subQ2=makeQuery(id+"F0.imprint","INTERSECT",VERTEX,{"disambiguationData":[OD(0.0)],"derivedFrom":[subQ1,subQ0]});Q3=makeQuery(id+"F0.imprint","IMPRINT",FACE,{"disambiguationData":[TD([[makeQuery(id+"F0.imprint","IMPRINT",EDGE,{"disambiguationData":[TD([[subQ2,-1.0]])],"derivedFrom":subQ1}),-1.0]])]});}
            var Q4;
            {var subQ0=sQuery(id+"F0.wireOp",EDGE,"E24");var subQ1=sQuery(id+"F0.wireOp",EDGE,"E2");var subQ2=makeQuery(id+"F0.imprint","INTERSECT",VERTEX,{"derivedFrom":[subQ1,subQ0]});Q4=makeQuery(id+"F0.imprint","IMPRINT",FACE,{"disambiguationData":[TD([[makeQuery(id+"F0.imprint","IMPRINT",EDGE,{"disambiguationData":[TD([[subQ2,-1.0]])],"derivedFrom":subQ1}),-1.0]])]});}
            var Q5;
            {var subQ0=sQuery(id+"F0.wireOp",EDGE,"E8.left");var subQ1=sQuery(id+"F0.wireOp",EDGE,"E2");var subQ2=makeQuery(id+"F0.imprint","INTERSECT",VERTEX,{"disambiguationData":[OD(1.0)],"derivedFrom":[subQ1,subQ0]});Q5=makeQuery(id+"F0.imprint","IMPRINT",FACE,{"disambiguationData":[TD([[makeQuery(id+"F0.imprint","IMPRINT",EDGE,{"disambiguationData":[TD([[subQ2,-1.0]])],"derivedFrom":subQ1}),-1.0]])]});}
            var Q6;
            {var subQ0=sQuery(id+"F0.wireOp",EDGE,"E8.top");var subQ1=sQuery(id+"F0.wireOp",EDGE,"E2");var subQ2=makeQuery(id+"F0.imprint","INTERSECT",VERTEX,{"derivedFrom":[subQ1,subQ0]});Q6=makeQuery(id+"F0.imprint","IMPRINT",FACE,{"disambiguationData":[TD([[makeQuery(id+"F0.imprint","IMPRINT",EDGE,{"disambiguationData":[TD([[subQ2,-1.0]])],"derivedFrom":subQ1}),-1.0]])]});}
            var Q7;
            {var subQ0=sQuery(id+"F0.wireOp",EDGE,"E16");var subQ1=sQuery(id+"F0.wireOp",EDGE,"E2");var subQ2=makeQuery(id+"F0.imprint","INTERSECT",VERTEX,{"derivedFrom":[subQ1,subQ0]});Q7=makeQuery(id+"F0.imprint","IMPRINT",FACE,{"disambiguationData":[TD([[makeQuery(id+"F0.imprint","IMPRINT",EDGE,{"disambiguationData":[TD([[subQ2,-1.0]])],"derivedFrom":subQ1}),-1.0]])]});}
            var Q8;
            {var subQ0=sQuery(id+"F0.wireOp",EDGE,"E22");var subQ1=sQuery(id+"F0.wireOp",EDGE,"E2");var subQ2=makeQuery(id+"F0.imprint","INTERSECT",VERTEX,{"disambiguationData":[OD(1.0)],"derivedFrom":[subQ1,subQ0]});Q8=makeQuery(id+"F0.imprint","IMPRINT",FACE,{"disambiguationData":[TD([[makeQuery(id+"F0.imprint","IMPRINT",EDGE,{"disambiguationData":[TD([[subQ2,-1.0]])],"derivedFrom":subQ1}),-1.0]])]});}
            var Q9;
            {var subQ0=sQuery(id+"F0.wireOp",EDGE,"E9.left");var subQ1=sQuery(id+"F0.wireOp",EDGE,"E2");var subQ2=makeQuery(id+"F0.imprint","INTERSECT",VERTEX,{"derivedFrom":[subQ1,subQ0]});Q9=makeQuery(id+"F0.imprint","IMPRINT",FACE,{"disambiguationData":[TD([[makeQuery(id+"F0.imprint","IMPRINT",EDGE,{"disambiguationData":[TD([[subQ2,-1.0]])],"derivedFrom":subQ1}),-1.0]])]});}
            var Q10;
            {var subQ0=sQuery(id+"F0.wireOp",EDGE,"E9.bottom");var subQ1=sQuery(id+"F0.wireOp",EDGE,"E2");var subQ2=makeQuery(id+"F0.imprint","INTERSECT",VERTEX,{"disambiguationData":[OD(1.0)],"derivedFrom":[subQ1,subQ0]});Q10=makeQuery(id+"F0.imprint","IMPRINT",FACE,{"disambiguationData":[TD([[makeQuery(id+"F0.imprint","IMPRINT",EDGE,{"disambiguationData":[TD([[subQ2,-1.0]])],"derivedFrom":subQ1}),-1.0]])]});}
            var Q11;
            {var subQ0=sQuery(id+"F0.wireOp",EDGE,"E21");var subQ1=sQuery(id+"F0.wireOp",EDGE,"E2");var subQ2=makeQuery(id+"F0.imprint","INTERSECT",VERTEX,{"derivedFrom":[subQ1,subQ0]});Q11=makeQuery(id+"F0.imprint","IMPRINT",FACE,{"disambiguationData":[TD([[makeQuery(id+"F0.imprint","IMPRINT",EDGE,{"disambiguationData":[TD([[subQ2,-1.0]])],"derivedFrom":subQ1}),-1.0]])]});}
            var Q12;
            {var subQ0=sQuery(id+"F0.wireOp",EDGE,"E23");var subQ1=sQuery(id+"F0.wireOp",EDGE,"E2");var subQ2=makeQuery(id+"F0.imprint","INTERSECT",VERTEX,{"disambiguationData":[OD(0.0)],"derivedFrom":[subQ1,subQ0]});Q12=makeQuery(id+"F0.imprint","IMPRINT",FACE,{"disambiguationData":[TD([[makeQuery(id+"F0.imprint","IMPRINT",EDGE,{"disambiguationData":[TD([[subQ2,-1.0]])],"derivedFrom":subQ1}),-1.0]])]});}
            var Q13;
            {var subQ0=sQuery(id+"F0.wireOp",EDGE,"E9.bottom");var subQ1=sQuery(id+"F0.wireOp",EDGE,"E2");var subQ2=makeQuery(id+"F0.imprint","INTERSECT",VERTEX,{"disambiguationData":[OD(0.0)],"derivedFrom":[subQ1,subQ0]});Q13=makeQuery(id+"F0.imprint","IMPRINT",FACE,{"disambiguationData":[TD([[makeQuery(id+"F0.imprint","IMPRINT",EDGE,{"disambiguationData":[TD([[subQ2,1.0]])],"derivedFrom":subQ1}),-1.0]])]});}
            var Q14;
            {var subQ0=sQuery(id+"F0.wireOp",EDGE,"E9.right");var subQ1=sQuery(id+"F0.wireOp",EDGE,"E2");var subQ2=makeQuery(id+"F0.imprint","INTERSECT",VERTEX,{"derivedFrom":[subQ1,subQ0]});Q14=makeQuery(id+"F0.imprint","IMPRINT",FACE,{"disambiguationData":[TD([[makeQuery(id+"F0.imprint","IMPRINT",EDGE,{"disambiguationData":[TD([[subQ2,1.0]])],"derivedFrom":subQ1}),-1.0]])]});}
            var Q15;
            {var subQ0=sQuery(id+"F0.wireOp",EDGE,"E18");var subQ1=sQuery(id+"F0.wireOp",EDGE,"E2");var subQ2=makeQuery(id+"F0.imprint","INTERSECT",VERTEX,{"derivedFrom":[subQ1,subQ0]});Q15=makeQuery(id+"F0.imprint","IMPRINT",FACE,{"disambiguationData":[TD([[makeQuery(id+"F0.imprint","IMPRINT",EDGE,{"disambiguationData":[TD([[subQ2,-1.0]])],"derivedFrom":subQ1}),-1.0]])]});}
            var Q16;
            {var subQ0=sQuery(id+"F0.wireOp",EDGE,"E26");var subQ1=sQuery(id+"F0.wireOp",EDGE,"E2");var subQ2=makeQuery(id+"F0.imprint","INTERSECT",VERTEX,{"disambiguationData":[OD(1.0)],"derivedFrom":[subQ1,subQ0]});Q16=makeQuery(id+"F0.imprint","IMPRINT",FACE,{"disambiguationData":[TD([[makeQuery(id+"F0.imprint","IMPRINT",EDGE,{"disambiguationData":[TD([[subQ2,-1.0]])],"derivedFrom":subQ1}),-1.0]])]});}
            extrude(context, id + "F2", {"entities" : qUnion([Q0, Q1, Q2, Q3, Q4, Q5, Q6, Q7, Q8, Q9, Q10, Q11, Q12, Q13, Q14, Q15, Q16]), "operationType" : NewBodyOperationType.ADD, "endBound" : BoundingType.SYMMETRIC, "depth" : 20 * mm});
        }
        {
            var Q0;
            Q0=makeQuery(id+"F1.opExtrude","CAP_EDGE",EDGE,{"disambiguationData":[OSD([sQuery(id+"F0.wireOp",EDGE,"E0")])],"isStart":false});
            chamfer(context, id + "F3", {"entities" : qUnion([Q0]), "width" : .5 * mm, "tangentPropagation" : true});
        }
    });
